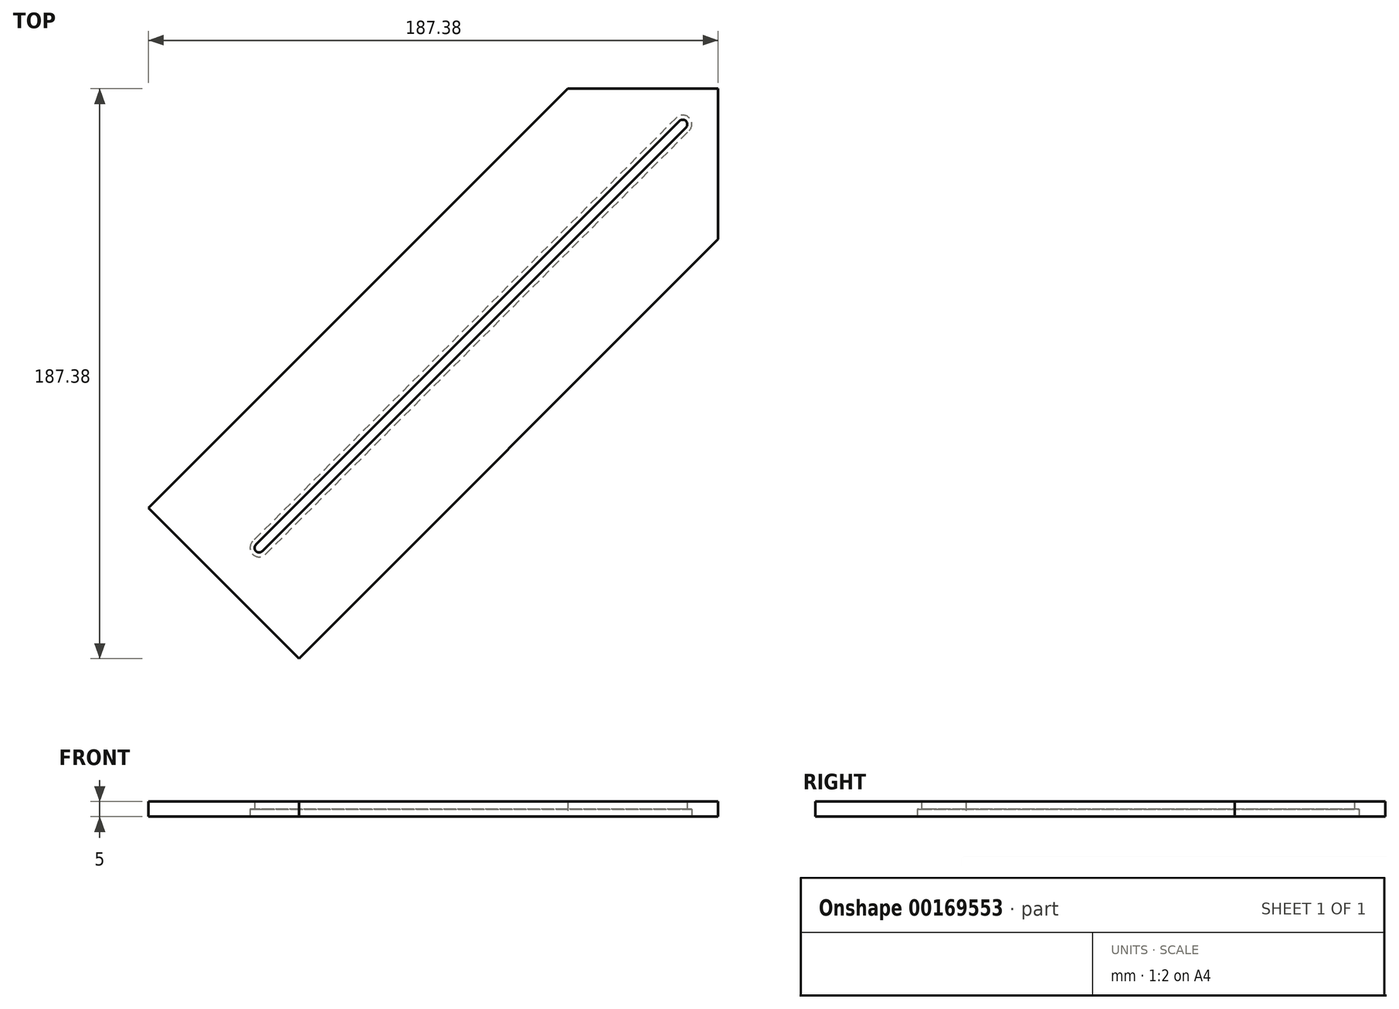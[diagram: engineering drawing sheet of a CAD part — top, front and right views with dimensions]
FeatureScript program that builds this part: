
annotation { "Feature Type Name" : "Feature", "Feature Type Description" : "" }
export const myFeature = defineFeature(function(context is Context, id is Id, definition is map)
    precondition{}
    {
        {
            var Q0;
            Q0=qCreatedBy(makeId("Top.planeOp"),FACE);
            var sketch = newSketch(context, id + "F0", { "sketchPlane" : qUnion([Q0])});
            skLineSegment(sketch, "E0", {"start": v(0, 0) * mm, "end": v(-49.5, 0) * mm, "construction": true});
            skLineSegment(sketch, "E1", {"start": v(-49.5, 0) * mm, "end": v(-187.38, -137.89) * mm});
            skLineSegment(sketch, "E2", {"start": v(-187.38, -137.89) * mm, "end": v(-137.89, -187.38) * mm});
            skLineSegment(sketch, "E3", {"start": v(-137.89, -187.38) * mm, "end": v(0, -49.5) * mm});
            skLineSegment(sketch, "E4", {"start": v(0, -49.5) * mm, "end": v(0, 0) * mm});
            skLineSegment(sketch, "E5", {"start": v(-149.9, -152.03) * mm, "end": v(-10.6, -12.73) * mm});
            skLineSegment(sketch, "E6", {"start": v(-12.73, -10.6) * mm, "end": v(-152.03, -149.9) * mm});
            skArc(sketch, "E7", {"start": v(-10.6, -12.73) * mm, "mid": v(-10.6, -10.6) * mm, "end": v(-12.73, -10.6) * mm});
            skArc(sketch, "E8", {"start": v(-152.03, -149.9) * mm, "mid": v(-152.03, -152.03) * mm, "end": v(-149.9, -152.03) * mm});
            skLineSegment(sketch, "E9", {"start": v(-11.67, -11.67) * mm, "end": v(0, 0) * mm, "construction": true});
            skLineSegment(sketch, "E10", {"start": v(-162.63, -162.63) * mm, "end": v(-150.97, -150.97) * mm, "construction": true});
            skLineSegment(sketch, "E11", {"start": v(-12.73, -10.6) * mm, "end": v(-10.6, -12.73) * mm, "construction": true});
            skLineSegment(sketch, "E12", {"start": v(-152.03, -149.9) * mm, "end": v(-149.9, -152.03) * mm, "construction": true});
            skLineSegment(sketch, "E13", {"start": v(-162.63, -162.63) * mm, "end": v(0, 0) * mm, "construction": true});
            skLineSegment(sketch, "E14", {"start": v(-20, 0) * mm, "end": v(0, 0) * mm});
            skLineSegment(sketch, "E15", {"start": v(-49.5, 0) * mm, "end": v(0, 0) * mm});
            skLineSegment(sketch, "E16", {"start": v(0, 0) * mm, "end": v(0, -49.5) * mm});
            skLineSegment(sketch, "E17.0", {"start": v(-13.79, -9.55) * mm, "end": v(-153.09, -148.85) * mm});
            skArc(sketch, "E17.1", {"start": v(-9.55, -13.79) * mm, "mid": v(-9.55, -9.55) * mm, "end": v(-13.79, -9.55) * mm});
            skLineSegment(sketch, "E17.2", {"start": v(-148.85, -153.09) * mm, "end": v(-9.55, -13.79) * mm});
            skArc(sketch, "E17.3", {"start": v(-153.09, -148.85) * mm, "mid": v(-153.09, -153.09) * mm, "end": v(-148.85, -153.09) * mm});
            skSolve(sketch);
        }
        {
            var Q0;
            {var subQ2=sQuery(id+"F0.wireOp",EDGE,"E1");Q0=makeQuery(id+"F0.imprint","IMPRINT",FACE,{"disambiguationData":[TD([[makeQuery(id+"F0.imprint","IMPRINT",EDGE,{"derivedFrom":subQ2}),1.0]])]});}
            var Q1;
            Q1=makeQuery(id+"F0.imprint","IMPRINT",FACE,{"disambiguationData":[TD([[makeQuery(id+"F0.imprint","IMPRINT",EDGE,{"derivedFrom":sQuery(id+"F0.wireOp",EDGE,"E5")}),-1.0]])]});
            extrude(context, id + "F1", {"entities" : qUnion([Q0, Q1]), "depth" : 5 * mm});
        }
        {
            var Q0;
            Q0=makeQuery(id+"F0.imprint","IMPRINT",FACE,{"disambiguationData":[TD([[makeQuery(id+"F0.imprint","IMPRINT",EDGE,{"derivedFrom":sQuery(id+"F0.wireOp",EDGE,"E5")}),-1.0]])]});
            extrude(context, id + "F2", {"entities" : qUnion([Q0]), "operationType" : NewBodyOperationType.REMOVE, "depth" : 2.5 * mm});
        }
    });
